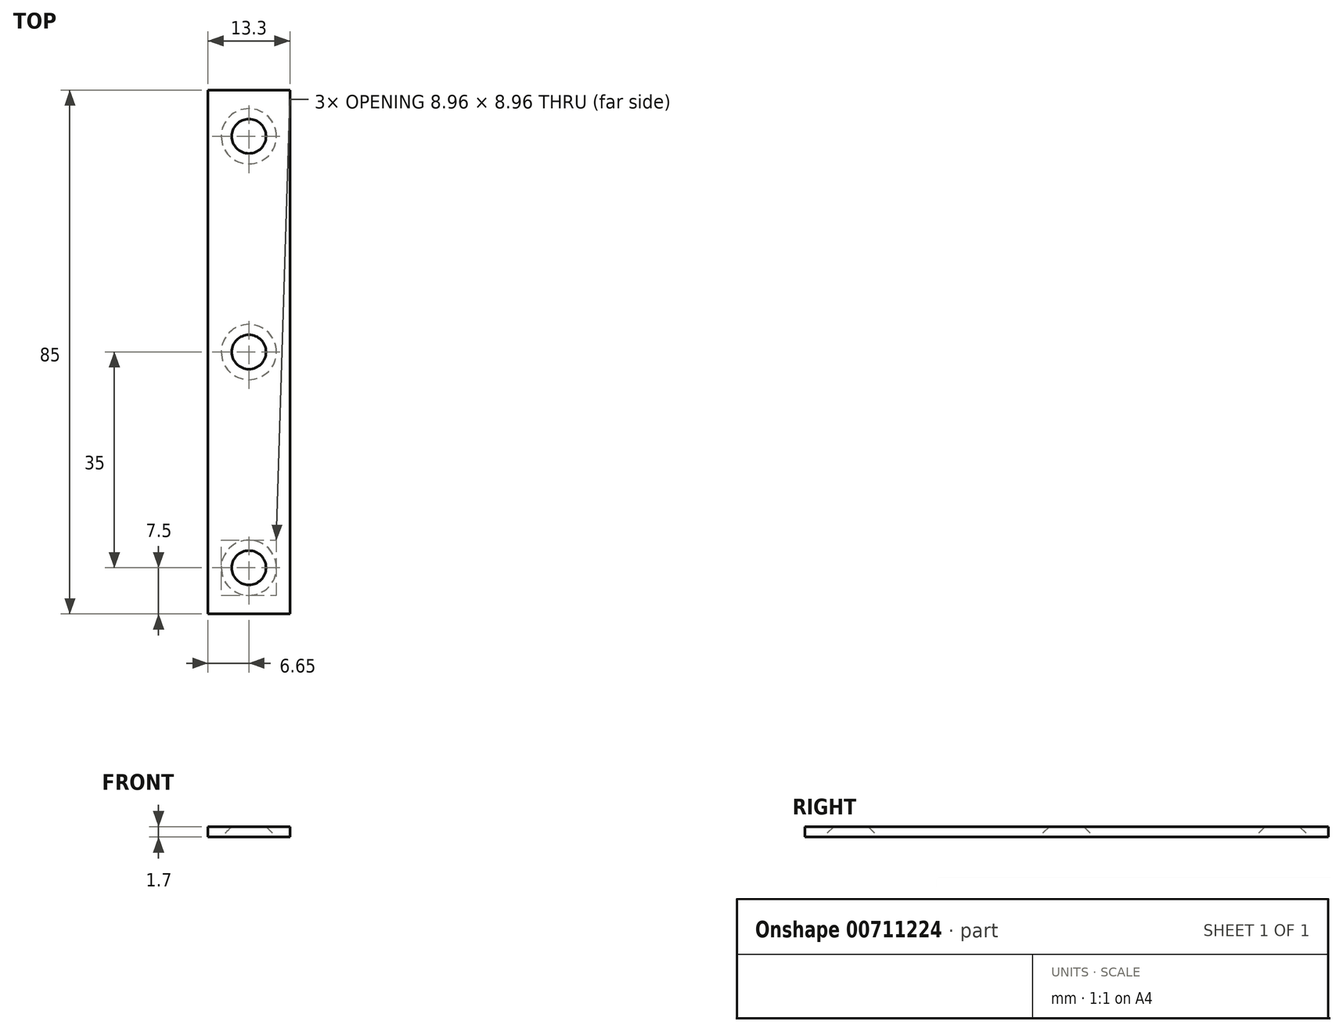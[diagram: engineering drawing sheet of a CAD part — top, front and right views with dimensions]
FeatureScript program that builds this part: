
annotation { "Feature Type Name" : "Feature", "Feature Type Description" : "" }
export const myFeature = defineFeature(function(context is Context, id is Id, definition is map)
    precondition{}
    {
        {
            var Q0;
            Q0=qCreatedBy(makeId("Front.planeOp"),FACE);
            var sketch = newSketch(context, id + "F0", { "sketchPlane" : qUnion([Q0])});
            skLineSegment(sketch, "E0.bottom", {"start": v(6.65, 0.85) * mm, "end": v(-6.65, 0.85) * mm});
            skLineSegment(sketch, "E0.top", {"start": v(6.65, -0.85) * mm, "end": v(-6.65, -0.85) * mm});
            skLineSegment(sketch, "E0.left", {"start": v(6.65, 0.85) * mm, "end": v(6.65, -0.85) * mm});
            skLineSegment(sketch, "E0.right", {"start": v(-6.65, 0.85) * mm, "end": v(-6.65, -0.85) * mm});
            skPoint(sketch, "E0.middle", {"position": v(0, 0) * mm});
            skLineSegment(sketch, "E1.bottom", {"start": v(4.4, 0.85) * mm, "end": v(-4.4, 0.85) * mm});
            skLineSegment(sketch, "E1.top", {"start": v(4.4, 4.15) * mm, "end": v(-4.4, 4.15) * mm});
            skLineSegment(sketch, "E1.left", {"start": v(4.4, 0.85) * mm, "end": v(4.4, 4.15) * mm});
            skLineSegment(sketch, "E1.right", {"start": v(-4.4, 0.85) * mm, "end": v(-4.4, 4.15) * mm});
            skPoint(sketch, "E1.middle", {"position": v(0, 2.5) * mm});
            skPoint(sketch, "E1.middle.positionSnap0", {"position": v(0, 0.85) * mm});
            skPoint(sketch, "E1.centerSnap0", {"position": v(0, 0.85) * mm});
            skSolve(sketch);
        }
        {
            var Q0;
            Q0=makeQuery(id+"F0.imprint","IMPRINT",FACE,{"disambiguationData":[TD([[makeQuery(id+"F0.imprint","IMPRINT",EDGE,{"derivedFrom":sQuery(id+"F0.wireOp",EDGE,"E0.top")}),-1.0]])]});
            var Q1;
            Q1=makeQuery(id+"F0.imprint","IMPRINT",FACE,{"disambiguationData":[TD([[makeQuery(id+"F0.imprint","IMPRINT",EDGE,{"derivedFrom":sQuery(id+"F0.wireOp",EDGE,"E1.bottom")}),-1.0]])]});
            extrude(context, id + "F1", {"entities" : qUnion([Q0, Q1]), "depth" : 85 * mm, "offsetDistance" : 25 * mm, "symmetric" : true});
        }
        {
            var Q0;
            Q0=makeQuery(id+"F1.opExtrude","SWEPT_FACE",FACE,{"disambiguationData":[OSD([sQuery(id+"F0.wireOp",EDGE,"E0.top")])]});
            var sketch = newSketch(context, id + "F2", { "sketchPlane" : qUnion([Q0])});
            skLineSegment(sketch, "E2", {"start": v(0, 0) * mm, "end": v(0, -35) * mm});
            skLineSegment(sketch, "E3", {"start": v(0, 0) * mm, "end": v(0, 35) * mm});
            skSolve(sketch);
        }
        {
            var Q0;
            Q0=sQuery(id+"F2.wireOp",VERTEX,"E2.end");
            var Q1;
            Q1=sQuery(id+"F2.wireOp",VERTEX,"E3.start");
            var Q2;
            Q2=sQuery(id+"F2.wireOp",VERTEX,"E3.end");
            var Q3;
            Q3=makeQuery(id+"F1.opExtrude","SWEPT_BODY",BODY,{"disambiguationData":[OSD([sQuery(id+"F0.wireOp",EDGE,"E0.bottom"),sQuery(id+"F0.wireOp",EDGE,"E0.top"),sQuery(id+"F0.wireOp",EDGE,"E0.left"),sQuery(id+"F0.wireOp",EDGE,"E0.right"),sQuery(id+"F0.wireOp",EDGE,"E1.top"),sQuery(id+"F0.wireOp",EDGE,"E1.left"),sQuery(id+"F0.wireOp",EDGE,"E1.right")])]});
            hole(context, id + "F3", {"style" : HoleStyle.C_SINK, "endStyle" : HoleEndStyle.THROUGH, "standardTappedOrClearance" : lookupTablePath({ "standard" : "ISO", "fit" : "Normal", "size" : "M4", "type" : "Clearance" }), "standardBlindInLast" : lookupTablePath({ "fit" : "Standard", "standard" : "ISO", "size" : "M4", "type" : "Clearance" }), "holeDiameter" : 4.4 * mm, "cSinkDiameter" : 8.96 * mm, "cSinkAngle" : 90 * degree, "majorDiameter" : 5 * mm, "isTappedThrough" : true, "tappedDepth" : 12 * mm, "tapClearance" : 3, "locations" : qUnion([Q0, Q1, Q2]), "scope" : qUnion([Q3]), "startStyle" : HoleStartStyle.SKETCH});
        }
    });
